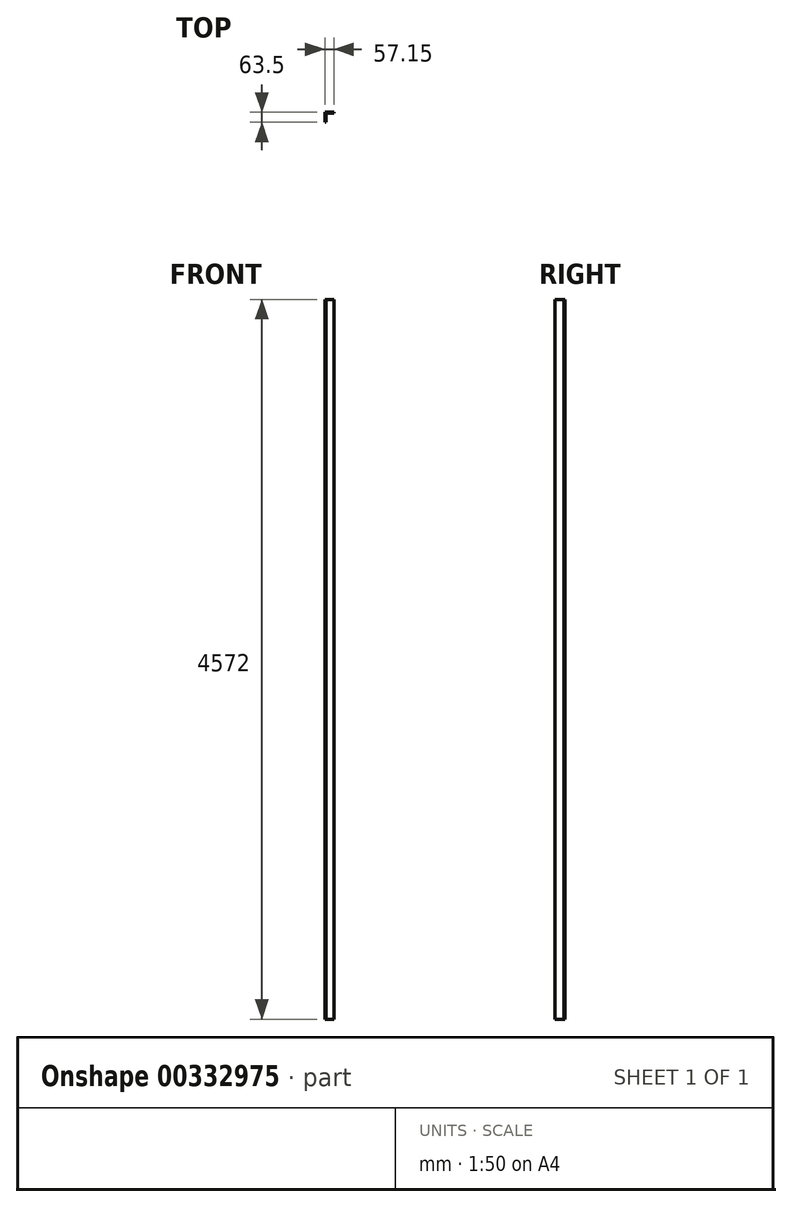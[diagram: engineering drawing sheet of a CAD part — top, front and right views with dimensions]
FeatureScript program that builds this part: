
annotation { "Feature Type Name" : "Feature", "Feature Type Description" : "" }
export const myFeature = defineFeature(function(context is Context, id is Id, definition is map)
    precondition{}
    {
        {
            var Q0;
            Q0=qCreatedBy(makeId("Top.planeOp"),FACE);
            var sketch = newSketch(context, id + "F0", { "sketchPlane" : qUnion([Q0])});
            skLineSegment(sketch, "E0", {"start": v(57.15, 57.15) * mm, "end": v(6.35, 57.15) * mm});
            skLineSegment(sketch, "E1", {"start": v(6.35, 57.15) * mm, "end": v(6.35, 0) * mm});
            skLineSegment(sketch, "E2", {"start": v(0, 0) * mm, "end": v(0, 63.5) * mm});
            skLineSegment(sketch, "E3", {"start": v(0, 63.5) * mm, "end": v(57.15, 63.5) * mm});
            skLineSegment(sketch, "E4", {"start": v(57.15, 63.5) * mm, "end": v(57.15, 57.15) * mm});
            skLineSegment(sketch, "E5", {"start": v(6.35, 0) * mm, "end": v(0, 0) * mm});
            skSolve(sketch);
        }
        {
            var Q0;
            Q0 = qSketchRegion(id + "F0", true);
            extrude(context, id + "F1", {"entities" : qUnion([Q0]), "depth" : 4572 * mm});
        }
    });
